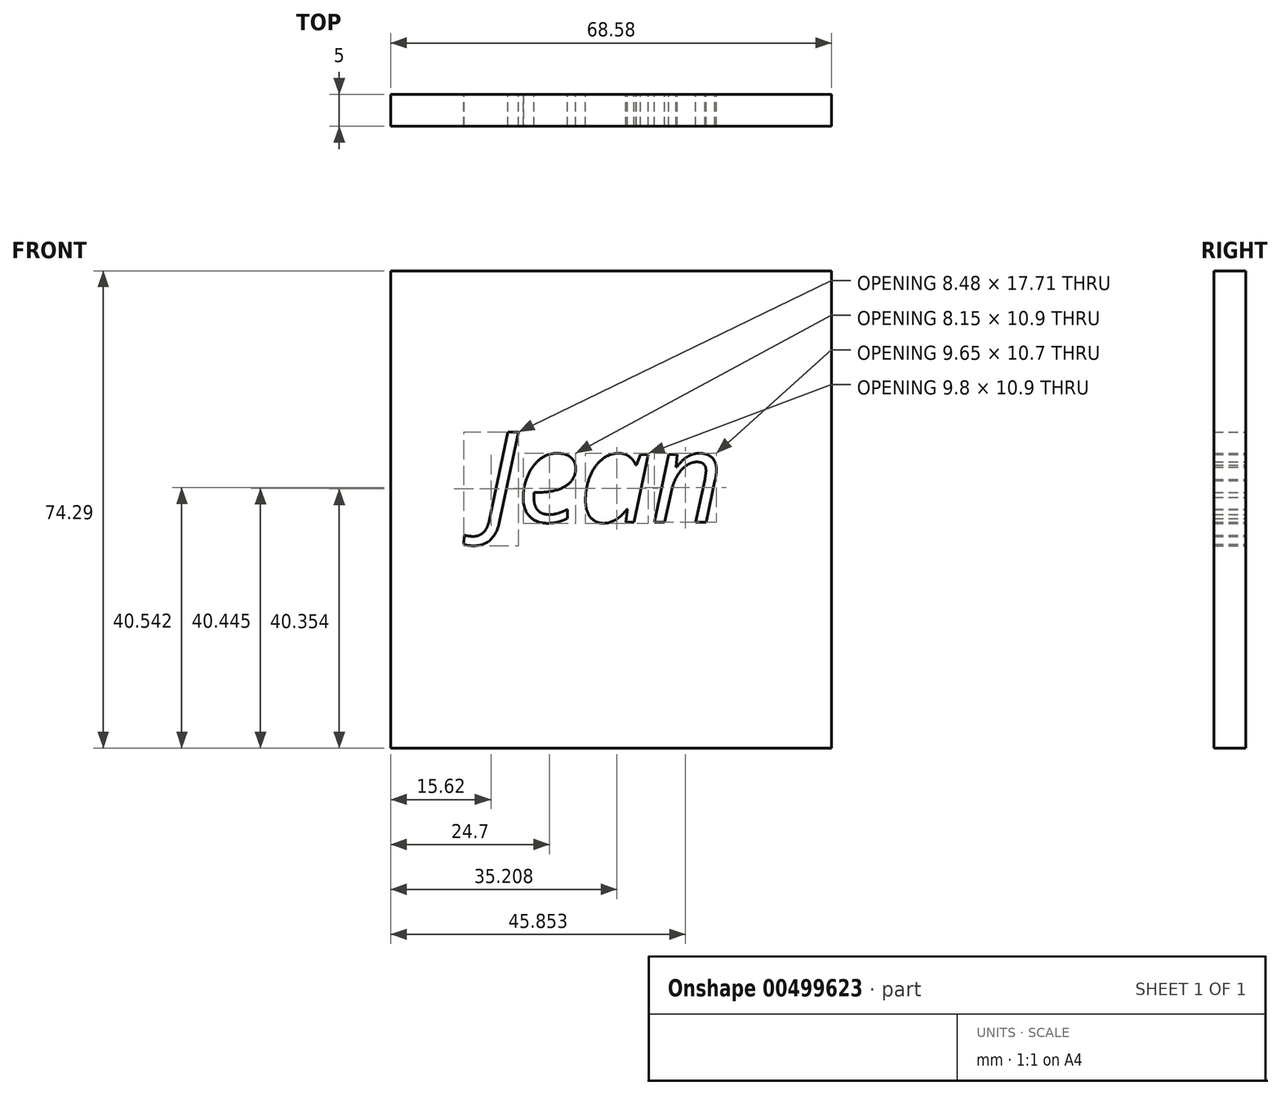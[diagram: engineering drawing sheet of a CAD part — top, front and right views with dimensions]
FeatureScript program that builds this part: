
annotation { "Feature Type Name" : "Feature", "Feature Type Description" : "" }
export const myFeature = defineFeature(function(context is Context, id is Id, definition is map)
    precondition{}
    {
        {
            var Q0;
            Q0=qCreatedBy(makeId("Front.planeOp"),FACE);
            var sketch = newSketch(context, id + "F0", { "sketchPlane" : qUnion([Q0])});
            skLineSegment(sketch, "E0.bottom", {"start": v(-34.9, 31.88) * mm, "end": v(33.69, 31.88) * mm});
            skLineSegment(sketch, "E0.top", {"start": v(-34.9, -42.41) * mm, "end": v(33.69, -42.41) * mm});
            skLineSegment(sketch, "E0.left", {"start": v(-34.9, 31.88) * mm, "end": v(-34.9, -42.41) * mm});
            skLineSegment(sketch, "E0.right", {"start": v(33.69, 31.88) * mm, "end": v(33.69, -42.41) * mm});
            skText(sketch, "E1", { "text": "Jean", "fontName": "OpenSans-Italic.ttf"});
            const initialGuessF0  = {"E1": [-0.02045, -0.00722, 1, 0, 0.01414]};
            skSetInitialGuess(sketch, initialGuessF0);
            skSolve(sketch);
        }
        {
            var Q0;
            Q0 = qSketchRegion(id + "F0", true);
            extrude(context, id + "F1", {"entities" : qUnion([Q0]), "depth" : 5 * mm});
        }
    });
